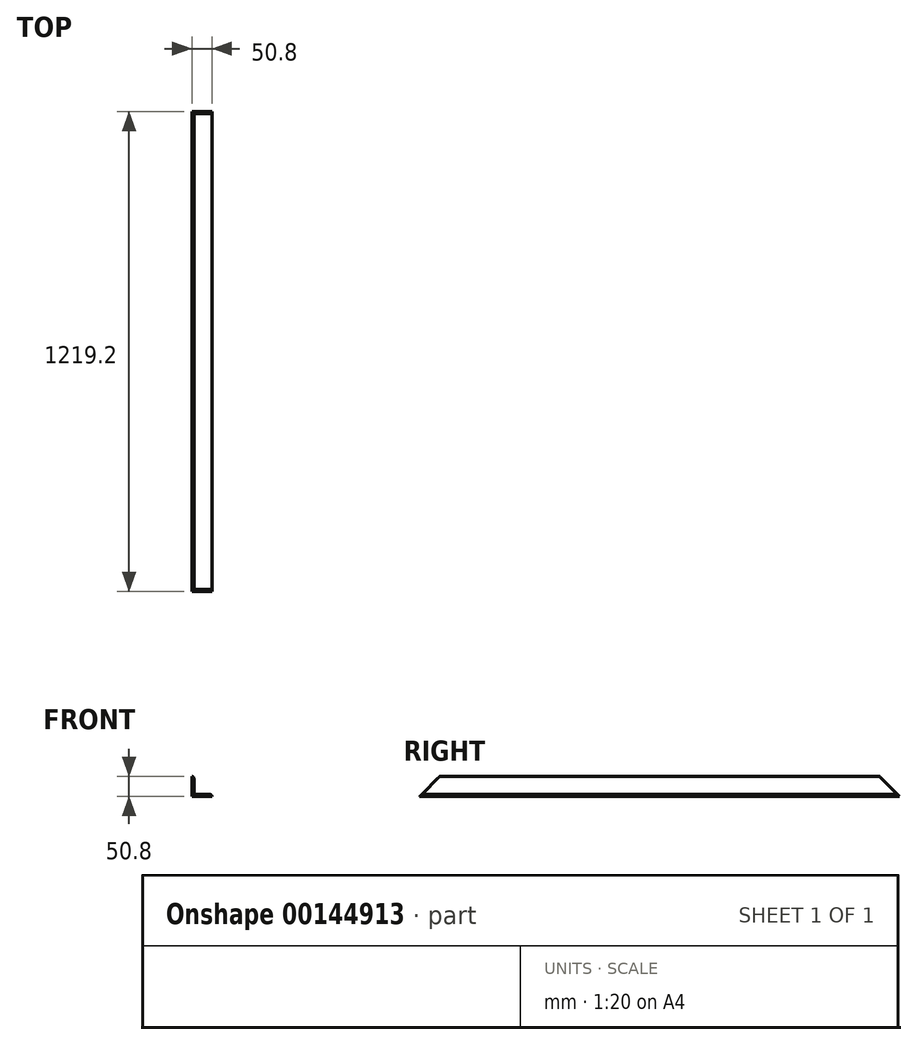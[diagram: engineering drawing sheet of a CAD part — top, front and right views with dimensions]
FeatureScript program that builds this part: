
annotation { "Feature Type Name" : "Feature", "Feature Type Description" : "" }
export const myFeature = defineFeature(function(context is Context, id is Id, definition is map)
    precondition{}
    {
        {
            var Q0;
            Q0=qCreatedBy(makeId("Front.planeOp"),FACE);
            var sketch = newSketch(context, id + "F0", { "sketchPlane" : qUnion([Q0])});
            skLineSegment(sketch, "E0", {"start": v(0, 0) * mm, "end": v(0, -50.8) * mm});
            skLineSegment(sketch, "E1", {"start": v(0, -50.8) * mm, "end": v(50.8, -50.8) * mm});
            skLineSegment(sketch, "E2", {"start": v(50.8, -50.8) * mm, "end": v(50.8, -50.8) * mm});
            skLineSegment(sketch, "E3", {"start": v(46.04, -46.04) * mm, "end": v(9.53, -46.04) * mm});
            skLineSegment(sketch, "E4", {"start": v(4.76, -41.27) * mm, "end": v(4.76, -4.76) * mm});
            skLineSegment(sketch, "E5", {"start": v(0, 0) * mm, "end": v(0, 0) * mm});
            skPoint(sketch, "E6.visualSharp", {"position": v(4.76, -46.04) * mm});
            skArc(sketch, "E6.filletArc", {"start": v(4.76, -41.27) * mm, "mid": v(6.16, -44.64) * mm, "end": v(9.53, -46.04) * mm});
            skPoint(sketch, "E7.visualSharp", {"position": v(4.76, 0) * mm});
            skArc(sketch, "E7.filletArc", {"start": v(4.76, -4.76) * mm, "mid": v(3.37, -1.4) * mm, "end": v(0, 0) * mm});
            skPoint(sketch, "E8.visualSharp", {"position": v(50.8, -46.04) * mm});
            skArc(sketch, "E8.filletArc", {"start": v(50.8, -50.8) * mm, "mid": v(49.4, -47.43) * mm, "end": v(46.04, -46.04) * mm});
            skSolve(sketch);
        }
        {
            var Q0;
            Q0=makeQuery(id+"F0.imprint","IMPRINT",FACE,{"disambiguationData":[TD([[makeQuery(id+"F0.imprint","IMPRINT",EDGE,{"derivedFrom":sQuery(id+"F0.wireOp",EDGE,"E0")}),1.0]])]});
            extrude(context, id + "F1", {"entities" : qUnion([Q0]), "oppositeDirection" : true, "depth" : 1219.2 * mm});
        }
        {
            var Q0;
            Q0=makeQuery(id+"F1.opExtrude","SWEPT_FACE",FACE,{"disambiguationData":[OSD([sQuery(id+"F0.wireOp",EDGE,"E0")])]});
            var sketch = newSketch(context, id + "F2", { "sketchPlane" : qUnion([Q0])});
            skLineSegment(sketch, "E9", {"start": v(0, -50.8) * mm, "end": v(-50.8, 0) * mm});
            skLineSegment(sketch, "E10", {"start": v(-50.8, 0) * mm, "end": v(0, 0) * mm});
            skLineSegment(sketch, "E11", {"start": v(0, 0) * mm, "end": v(0, -50.8) * mm});
            skLineSegment(sketch, "E12", {"start": v(-1219.2, -50.8) * mm, "end": v(-1168.4, 0) * mm});
            skLineSegment(sketch, "E13", {"start": v(-1168.4, 0) * mm, "end": v(-1219.2, 0) * mm});
            skLineSegment(sketch, "E14", {"start": v(-1219.2, 0) * mm, "end": v(-1219.2, -50.8) * mm});
            skSolve(sketch);
        }
        {
            var Q0;
            Q0 = qSketchRegion(id + "F2", true);
            extrude(context, id + "F3", {"entities" : qUnion([Q0]), "operationType" : NewBodyOperationType.REMOVE, "oppositeDirection" : true, "depth" : 50.8 * mm});
        }
    });
